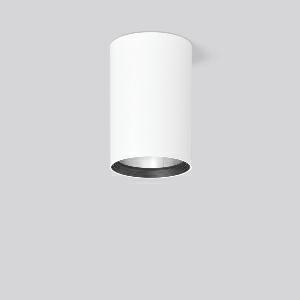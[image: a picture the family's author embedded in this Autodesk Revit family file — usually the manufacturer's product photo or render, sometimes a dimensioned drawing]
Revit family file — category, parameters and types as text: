
# Revit family: heledon_maxi_a_931216_002_2_76_1a20
name_source: partatom
category: Lighting Fixtures
units: mm (PartAtom-declared; Revit-internal decimal feet)

## family parameters
Cut with Voids When Loaded = No
Host = Face
Light Source = No
Part Type = Normal
Room Calculation Point = No
Round Connector Dimension = Use Diameter
Shared = No

## types (1)
- HELEDON maxi A (1 x LED Modul 927, 3050 lm, 2700)
    Apparent Load = 25 VA
    Approval mark = CE
    CIE Flux Codes = 100 100 100 100 100
    Color Rendering = 92
    Color Temperature = 2700
    Default Elevation = 1800 mm
    Description = Series: HELEDON maxi
Cylindrical surface-mounted downlight. Housing: die-cast aluminium, powder-coated. Internal ceiling frame polycarbonate with bayonet mounting. Black plastic ring and recessed LED to prevent glare from the side. Optical assembly with reflector made of MIRO-Silver with 98% total light reflection for outstanding efficiency - can be changed without tools. Best colour rendering index Ra>90. Suitable for Ceiling mounting. Easy installation with a separate ceiling frame with bayonet mounting and plug connection. Driver integrated. Connected via plug-in connector. High quality converter without flickering and stroboscopic effect. The following accessories can be mounted without use of tools: interchangeable lenses, decorative glasses, honeycomb louvre, clear and frosted diffusers, white interchangeable plastic ring. 
Colour: traffic white, matt (RAL 9016)
Diameter: 123 mm
Height: 183 mm
Lamp: LED
Socket: without socket
Colour temperature: 2700K
Colour rendering index (CRI): 92
System power: 25 W
Rated luminous flux: 3050 lm
Luminous efficiency: 122 lm/W
Control gear: Converter, dimmable, DALI
Protection class: I
Type of protection: IP 20
    Height = 183 mm
    Lamp = 1 x LED Modul 927
    Lamp Light Flux = 3050 lm
    Lamp count = 1
    Length = 123 mm
    Lifetime = 50000 h
    Luminous efficacy = 122 lm/W
    Manufacturer = RZB
    ModVariant = No
    Model = 931216.002.2.76
    Mounting Place = Ceiling
    Mounting Type = Surface mounted
    Number of Poles = 1
    OnlyDefault = Yes
    Power Factor = 1
    Product Name = HELEDON maxi A
    Product group = Surface mounted downlights
    ProductGroupID = 302
    Protection Class = Protection class I
    Protection Degree = IP 20
    RLX_Detail_Level = 1
    RLX_Emergency_Light_Flux = 0 lm
    RLX_Emergency_Type = 0
    RLX_Emergency_Type_DB = No
    RlxData = <blob elided: 99145 chars, md5=3b3149b8>
    Socket = socket
    Standby Power = 0 W
    System Light Flux = 3050 lm
    System Power = 25 W
    Type Comments = Product without accessories
    Type Image = 931192.002.jpg
    URL = http://relux.com
    VarID = ---
    Voltage = 230 V
    Voltage Range = 220-240 V
    Weight = 0.00 kg
    Width = 0 mm  [stored 0 ft]

note: [stored X ft] marks values corroborated as IEEE doubles in the binary element streams (Revit-internal decimal feet)

## geometry (parser evidence)
native form markers: Blend x4, Sweep x10
no freeform markers — native parametric forms only
